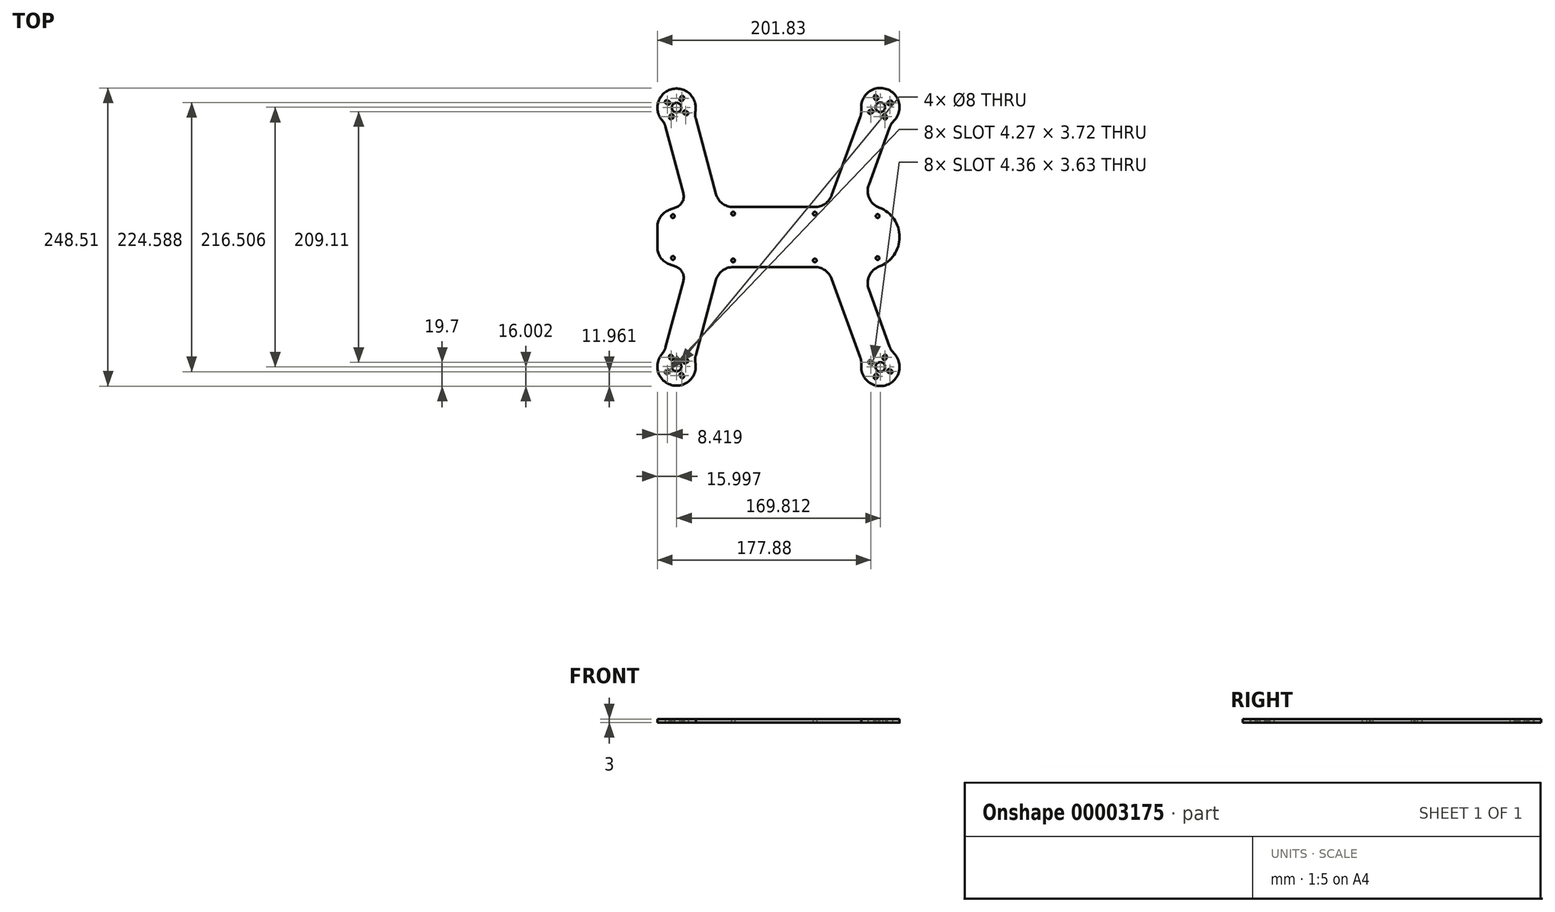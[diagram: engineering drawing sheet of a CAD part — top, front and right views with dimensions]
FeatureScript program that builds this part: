
annotation { "Feature Type Name" : "Feature", "Feature Type Description" : "" }
export const myFeature = defineFeature(function(context is Context, id is Id, definition is map)
    precondition{}
    {
        {
            var Q0;
            Q0=qCreatedBy(makeId("Top.planeOp"),FACE);
            var sketch = newSketch(context, id + "F0", { "sketchPlane" : qUnion([Q0])});
            skLineSegment(sketch, "E0", {"start": v(-72.92, 96.67) * mm, "end": v(-4.93, 96.67) * mm});
            skLineSegment(sketch, "E1", {"start": v(9.17, 106.54) * mm, "end": v(32.94, 171.87) * mm});
            skLineSegment(sketch, "E2", {"start": v(34.3, 175.6) * mm, "end": v(58.74, 166.72) * mm});
            skLineSegment(sketch, "E3", {"start": v(57.38, 162.98) * mm, "end": v(40.04, 115.35) * mm});
            skLineSegment(sketch, "E4", {"start": v(40.04, 28) * mm, "end": v(57.38, -19.63) * mm});
            skLineSegment(sketch, "E5", {"start": v(58.74, -23.37) * mm, "end": v(34.3, -32.26) * mm});
            skLineSegment(sketch, "E6", {"start": v(32.94, -28.52) * mm, "end": v(9.17, 36.8) * mm});
            skLineSegment(sketch, "E7", {"start": v(-4.93, 46.67) * mm, "end": v(-72.92, 46.67) * mm});
            skLineSegment(sketch, "E8", {"start": v(-87.4, 35.56) * mm, "end": v(-104.1, -26.76) * mm});
            skLineSegment(sketch, "E9", {"start": v(-105.13, -30.6) * mm, "end": v(-130.25, -23.87) * mm});
            skLineSegment(sketch, "E10", {"start": v(-129.22, -20.03) * mm, "end": v(-114.47, 35) * mm});
            skLineSegment(sketch, "E11", {"start": v(-114.47, 108.35) * mm, "end": v(-129.22, 163.38) * mm});
            skLineSegment(sketch, "E12", {"start": v(-130.25, 167.22) * mm, "end": v(-105.13, 173.95) * mm});
            skLineSegment(sketch, "E13", {"start": v(-104.11, 170.14) * mm, "end": v(-87.4, 107.8) * mm});
            skPoint(sketch, "E14.visualSharp", {"position": v(5.57, 96.67) * mm});
            skArc(sketch, "E14.filletArc", {"start": v(-4.93, 96.67) * mm, "mid": v(3.67, 99.39) * mm, "end": v(9.17, 106.54) * mm});
            skPoint(sketch, "E15.visualSharp", {"position": v(-84.43, 96.67) * mm});
            skArc(sketch, "E15.filletArc", {"start": v(-87.4, 107.8) * mm, "mid": v(-82.05, 99.77) * mm, "end": v(-72.92, 96.67) * mm});
            skPoint(sketch, "E16.visualSharp", {"position": v(-84.43, 46.67) * mm});
            skArc(sketch, "E16.filletArc", {"start": v(-72.92, 46.67) * mm, "mid": v(-82.05, 43.57) * mm, "end": v(-87.4, 35.56) * mm});
            skPoint(sketch, "E17.visualSharp", {"position": v(5.57, 46.67) * mm});
            skArc(sketch, "E17.filletArc", {"start": v(9.17, 36.8) * mm, "mid": v(3.67, 43.96) * mm, "end": v(-4.93, 46.67) * mm});
            skLineSegment(sketch, "E18", {"start": v(-135.56, 175.45) * mm, "end": v(-104.65, 183.73) * mm});
            skArc(sketch, "E19", {"start": v(-135.56, 175.45) * mm, "mid": v(-134.27, 172.15) * mm, "end": v(-132.28, 169.22) * mm});
            skArc(sketch, "E20", {"start": v(-104.39, 176.68) * mm, "mid": v(-104.15, 180.22) * mm, "end": v(-104.7, 183.72) * mm});
            skArc(sketch, "E21", {"start": v(-104.7, 183.72) * mm, "mid": v(-124.24, 194.94) * mm, "end": v(-135.56, 175.45) * mm});
            skPoint(sketch, "E22.visualSharp", {"position": v(-130.25, 167.22) * mm});
            skArc(sketch, "E22.filletArc", {"start": v(-129.22, 163.38) * mm, "mid": v(-130.43, 166.47) * mm, "end": v(-132.28, 169.22) * mm});
            skPoint(sketch, "E23.visualSharp", {"position": v(-105.13, 173.95) * mm});
            skArc(sketch, "E23.filletArc", {"start": v(-104.39, 176.68) * mm, "mid": v(-104.6, 173.4) * mm, "end": v(-104.11, 170.14) * mm});
            skLineSegment(sketch, "E24", {"start": v(34.67, 185.4) * mm, "end": v(64.74, 174.46) * mm});
            skArc(sketch, "E25", {"start": v(64.74, 174.46) * mm, "mid": v(55.18, 194.96) * mm, "end": v(34.67, 185.4) * mm});
            skArc(sketch, "E26", {"start": v(60.94, 168.53) * mm, "mid": v(63.17, 171.28) * mm, "end": v(64.74, 174.46) * mm});
            skArc(sketch, "E27", {"start": v(34.67, 185.4) * mm, "mid": v(33.84, 181.96) * mm, "end": v(33.78, 178.42) * mm});
            skPoint(sketch, "E28.visualSharp", {"position": v(34.3, 175.6) * mm});
            skArc(sketch, "E28.filletArc", {"start": v(32.94, 171.87) * mm, "mid": v(33.73, 175.1) * mm, "end": v(33.78, 178.42) * mm});
            skPoint(sketch, "E29.visualSharp", {"position": v(58.74, 166.72) * mm});
            skArc(sketch, "E29.filletArc", {"start": v(60.94, 168.53) * mm, "mid": v(58.85, 165.95) * mm, "end": v(57.38, 162.98) * mm});
            skLineSegment(sketch, "E30", {"start": v(34.67, -42.05) * mm, "end": v(64.74, -31.1) * mm});
            skArc(sketch, "E31", {"start": v(33.78, -35.07) * mm, "mid": v(33.84, -38.6) * mm, "end": v(34.67, -42.05) * mm});
            skArc(sketch, "E32", {"start": v(34.67, -42.05) * mm, "mid": v(55.18, -51.61) * mm, "end": v(64.74, -31.1) * mm});
            skArc(sketch, "E33", {"start": v(64.74, -31.1) * mm, "mid": v(63.17, -27.93) * mm, "end": v(60.94, -25.18) * mm});
            skPoint(sketch, "E34.visualSharp", {"position": v(58.74, -23.37) * mm});
            skArc(sketch, "E34.filletArc", {"start": v(57.38, -19.63) * mm, "mid": v(58.85, -22.6) * mm, "end": v(60.94, -25.18) * mm});
            skPoint(sketch, "E35.visualSharp", {"position": v(34.3, -32.26) * mm});
            skArc(sketch, "E35.filletArc", {"start": v(33.78, -35.07) * mm, "mid": v(33.73, -31.75) * mm, "end": v(32.94, -28.52) * mm});
            skLineSegment(sketch, "E36", {"start": v(-135.56, -32.1) * mm, "end": v(-104.65, -40.39) * mm});
            skArc(sketch, "E37", {"start": v(-135.56, -32.1) * mm, "mid": v(-124.24, -51.7) * mm, "end": v(-104.65, -40.39) * mm});
            skArc(sketch, "E38", {"start": v(-132.28, -25.87) * mm, "mid": v(-134.27, -28.8) * mm, "end": v(-135.56, -32.1) * mm});
            skArc(sketch, "E39", {"start": v(-104.65, -40.39) * mm, "mid": v(-104.12, -36.88) * mm, "end": v(-104.37, -33.35) * mm});
            skPoint(sketch, "E40.visualSharp", {"position": v(-130.25, -23.87) * mm});
            skArc(sketch, "E40.filletArc", {"start": v(-132.28, -25.87) * mm, "mid": v(-130.43, -23.12) * mm, "end": v(-129.22, -20.03) * mm});
            skPoint(sketch, "E41.visualSharp", {"position": v(-105.13, -30.6) * mm});
            skArc(sketch, "E41.filletArc", {"start": v(-104.1, -26.76) * mm, "mid": v(-104.6, -30.04) * mm, "end": v(-104.37, -33.35) * mm});
            skPoint(sketch, "E42.visualSharp", {"position": v(-112.13, 99.63) * mm});
            skPoint(sketch, "E43.visualSharp", {"position": v(-112.13, 43.72) * mm});
            skPoint(sketch, "E44", {"position": v(-123.13, 89.13) * mm});
            skCircle(sketch, "E45", {"center": v(-123.13, 89.13) * mm, "radius": 1.5 * mm});
            skPoint(sketch, "E46", {"position": v(-123.13, 54.22) * mm});
            skCircle(sketch, "E47", {"center": v(-123.13, 54.22) * mm, "radius": 1.5 * mm});
            skPoint(sketch, "E48", {"position": v(-72.92, 91.17) * mm});
            skCircle(sketch, "E49", {"center": v(-72.92, 91.17) * mm, "radius": 1.5 * mm});
            skPoint(sketch, "E50", {"position": v(-72.92, 52.17) * mm});
            skCircle(sketch, "E51", {"center": v(-72.92, 52.17) * mm, "radius": 1.5 * mm});
            skPoint(sketch, "E52", {"position": v(-4.93, 52.17) * mm});
            skCircle(sketch, "E53", {"center": v(-4.93, 52.17) * mm, "radius": 1.5 * mm});
            skPoint(sketch, "E54", {"position": v(-4.93, 91.17) * mm});
            skCircle(sketch, "E55", {"center": v(-4.93, 91.17) * mm, "radius": 1.5 * mm});
            skLineSegment(sketch, "E56", {"start": v(-113.43, 191.15) * mm, "end": v(-126.56, 168.41) * mm});
            skPoint(sketch, "E57", {"position": v(-124.1, 172.67) * mm});
            skPoint(sketch, "E58", {"position": v(-116.1, 186.52) * mm});
            skLineSegment(sketch, "E59", {"start": v(-131.69, -42.93) * mm, "end": v(-110.1, -30.47) * mm});
            skPoint(sketch, "E60", {"position": v(-113.17, -32.24) * mm});
            skPoint(sketch, "E61", {"position": v(-127.03, -40.24) * mm});
            skLineSegment(sketch, "E62", {"start": v(54.74, -25.78) * mm, "end": v(43.87, -49.1) * mm});
            skPoint(sketch, "E63", {"position": v(53.1, -29.33) * mm});
            skPoint(sketch, "E64", {"position": v(46.33, -43.83) * mm});
            skLineSegment(sketch, "E65", {"start": v(60.38, 184.9) * mm, "end": v(38.81, 174.85) * mm});
            skPoint(sketch, "E66", {"position": v(42.46, 176.55) * mm});
            skPoint(sketch, "E67", {"position": v(56.96, 183.3) * mm});
            skCircle(sketch, "E68", {"center": v(-116.1, 186.52) * mm, "radius": 1.5 * mm});
            skCircle(sketch, "E69", {"center": v(-124.1, 172.67) * mm, "radius": 1.5 * mm});
            skCircle(sketch, "E70", {"center": v(-120.1, 179.6) * mm, "radius": 4 * mm});
            skCircle(sketch, "E71", {"center": v(-113.17, -32.24) * mm, "radius": 1.5 * mm});
            skCircle(sketch, "E72", {"center": v(-120.1, -36.24) * mm, "radius": 4 * mm});
            skCircle(sketch, "E73", {"center": v(-127.03, -40.24) * mm, "radius": 1.5 * mm});
            skCircle(sketch, "E74", {"center": v(53.1, -29.33) * mm, "radius": 1.5 * mm});
            skCircle(sketch, "E75", {"center": v(49.7, -36.58) * mm, "radius": 4 * mm});
            skCircle(sketch, "E76", {"center": v(46.33, -43.83) * mm, "radius": 1.5 * mm});
            skCircle(sketch, "E77", {"center": v(49.7, 179.93) * mm, "radius": 4 * mm});
            skCircle(sketch, "E78", {"center": v(56.96, 183.3) * mm, "radius": 1.5 * mm});
            skCircle(sketch, "E79", {"center": v(42.46, 176.55) * mm, "radius": 1.5 * mm});
            skLineSegment(sketch, "E80", {"start": v(-136.08, 80.17) * mm, "end": v(-136.08, 63.17) * mm});
            skPoint(sketch, "E81", {"position": v(65.73, 71.67) * mm});
            skLineSegment(sketch, "E82", {"start": v(65.73, 71.67) * mm, "end": v(-136.08, 71.67) * mm});
            skPoint(sketch, "E83", {"position": v(-136.08, 89.67) * mm});
            skPoint(sketch, "E84", {"position": v(-136.08, 53.67) * mm});
            skLineSegment(sketch, "E85", {"start": v(-126.41, 94.2) * mm, "end": v(-120.58, 96.42) * mm});
            skLineSegment(sketch, "E86", {"start": v(-126.41, 49.15) * mm, "end": v(-120.58, 46.93) * mm});
            skArc(sketch, "E87.filletArc", {"start": v(-126.41, 94.2) * mm, "mid": v(-133.43, 88.69) * mm, "end": v(-136.08, 80.17) * mm});
            skArc(sketch, "E88.filletArc", {"start": v(-136.08, 63.17) * mm, "mid": v(-133.43, 54.66) * mm, "end": v(-126.41, 49.15) * mm});
            skArc(sketch, "E89.filletArc", {"start": v(-120.58, 96.42) * mm, "mid": v(-115.23, 101.2) * mm, "end": v(-114.47, 108.35) * mm});
            skArc(sketch, "E90.filletArc", {"start": v(-114.47, 35) * mm, "mid": v(-115.23, 42.14) * mm, "end": v(-120.58, 46.93) * mm});
            skPoint(sketch, "E91", {"position": v(-115.35, 187.82) * mm});
            skPoint(sketch, "E92", {"position": v(-124.85, 171.37) * mm});
            skCircle(sketch, "E93", {"center": v(-115.35, 187.82) * mm, "radius": 1.5 * mm});
            skCircle(sketch, "E94", {"center": v(-124.85, 171.37) * mm, "radius": 1.5 * mm});
            skLineSegment(sketch, "E95", {"start": v(-118.91, 184.66) * mm, "end": v(-115.69, 190.24) * mm});
            skLineSegment(sketch, "E96", {"start": v(-116.07, 183.57) * mm, "end": v(-113.34, 188.31) * mm});
            skLineSegment(sketch, "E97", {"start": v(-127.48, 169.81) * mm, "end": v(-125.06, 174.01) * mm});
            skLineSegment(sketch, "E98", {"start": v(-124.37, 169.2) * mm, "end": v(-122.64, 172.2) * mm});
            skPoint(sketch, "E99", {"position": v(58.32, 183.94) * mm});
            skPoint(sketch, "E100", {"position": v(41.1, 175.91) * mm});
            skCircle(sketch, "E101", {"center": v(41.1, 175.91) * mm, "radius": 1.5 * mm});
            skLineSegment(sketch, "E102", {"start": v(39.02, 176.6) * mm, "end": v(42.87, 178.4) * mm});
            skLineSegment(sketch, "E103", {"start": v(40.26, 173.87) * mm, "end": v(44.56, 175.87) * mm});
            skCircle(sketch, "E104", {"center": v(58.32, 183.94) * mm, "radius": 1.5 * mm});
            skLineSegment(sketch, "E105", {"start": v(54.7, 183.9) * mm, "end": v(58.65, 185.75) * mm});
            skLineSegment(sketch, "E106", {"start": v(56.18, 181.3) * mm, "end": v(60.7, 183.4) * mm});
            skPoint(sketch, "E107", {"position": v(53.72, -27.97) * mm});
            skCircle(sketch, "E108", {"center": v(53.72, -27.97) * mm, "radius": 1.5 * mm});
            skLineSegment(sketch, "E109", {"start": v(50.62, -31.07) * mm, "end": v(52.53, -26.98) * mm});
            skLineSegment(sketch, "E110", {"start": v(53.5, -32) * mm, "end": v(55.61, -27.47) * mm});
            skPoint(sketch, "E111", {"position": v(45.7, -45.19) * mm});
            skCircle(sketch, "E112", {"center": v(45.7, -45.19) * mm, "radius": 1.5 * mm});
            skLineSegment(sketch, "E113", {"start": v(43.25, -46.9) * mm, "end": v(45.34, -42.4) * mm});
            skLineSegment(sketch, "E114", {"start": v(46.2, -47.66) * mm, "end": v(48.31, -43.12) * mm});
            skPoint(sketch, "E115", {"position": v(-111.88, -31.5) * mm});
            skCircle(sketch, "E116", {"center": v(-111.88, -31.5) * mm, "radius": 1.5 * mm});
            skLineSegment(sketch, "E117", {"start": v(-116.41, -32.38) * mm, "end": v(-112.12, -29.9) * mm});
            skLineSegment(sketch, "E118", {"start": v(-114.3, -34.63) * mm, "end": v(-109.74, -32) * mm});
            skPoint(sketch, "E119", {"position": v(-128.33, -41) * mm});
            skCircle(sketch, "E120", {"center": v(-128.33, -41) * mm, "radius": 1.5 * mm});
            skLineSegment(sketch, "E121", {"start": v(-131.8, -41.27) * mm, "end": v(-127.15, -38.58) * mm});
            skLineSegment(sketch, "E122", {"start": v(-130, -43.7) * mm, "end": v(-124.48, -40.5) * mm});
            skArc(sketch, "E123", {"start": v(48.81, 47.15) * mm, "mid": v(65.73, 71.67) * mm, "end": v(48.81, 96.2) * mm});
            skPoint(sketch, "E124.visualSharp", {"position": v(33.43, 97.2) * mm});
            skArc(sketch, "E124.filletArc", {"start": v(40.04, 115.35) * mm, "mid": v(40.5, 103.98) * mm, "end": v(48.81, 96.2) * mm});
            skPoint(sketch, "E125.visualSharp", {"position": v(33.43, 46.15) * mm});
            skArc(sketch, "E125.filletArc", {"start": v(48.81, 47.15) * mm, "mid": v(40.5, 39.37) * mm, "end": v(40.04, 28) * mm});
            skPoint(sketch, "E126", {"position": v(-71.08, 71.67) * mm});
            skPoint(sketch, "E127", {"position": v(-67.08, 71.67) * mm});
            skPoint(sketch, "E128", {"position": v(42.92, 71.67) * mm});
            skPoint(sketch, "E129", {"position": v(46.73, 71.67) * mm});
            skPoint(sketch, "E130", {"position": v(-71.08, 89.67) * mm});
            skPoint(sketch, "E131", {"position": v(-71.08, 53.67) * mm});
            skLineSegment(sketch, "E132.bottom", {"start": v(-71.08, 53.67) * mm, "end": v(-131.08, 53.67) * mm});
            skLineSegment(sketch, "E132.top", {"start": v(-71.08, 89.67) * mm, "end": v(-131.08, 89.67) * mm});
            skLineSegment(sketch, "E132.left", {"start": v(-71.08, 53.67) * mm, "end": v(-71.08, 89.67) * mm});
            skLineSegment(sketch, "E132.right", {"start": v(-131.08, 53.67) * mm, "end": v(-131.08, 89.67) * mm});
            skLineSegment(sketch, "E133.bottom", {"start": v(-67.08, 53.67) * mm, "end": v(42.92, 53.67) * mm});
            skLineSegment(sketch, "E133.top", {"start": v(-67.08, 89.67) * mm, "end": v(42.92, 89.67) * mm});
            skLineSegment(sketch, "E133.left", {"start": v(-67.08, 53.67) * mm, "end": v(-67.08, 89.67) * mm});
            skLineSegment(sketch, "E133.right", {"start": v(42.92, 53.67) * mm, "end": v(42.92, 89.67) * mm});
            skPoint(sketch, "E134", {"position": v(-67.08, 53.67) * mm});
            skLineSegment(sketch, "E135.bottom", {"start": v(48.73, 66.67) * mm, "end": v(56.73, 66.67) * mm});
            skLineSegment(sketch, "E135.top", {"start": v(48.73, 76.67) * mm, "end": v(56.73, 76.67) * mm});
            skLineSegment(sketch, "E135.left", {"start": v(46.73, 68.67) * mm, "end": v(46.73, 74.67) * mm});
            skLineSegment(sketch, "E135.right", {"start": v(58.73, 68.67) * mm, "end": v(58.73, 74.67) * mm});
            skPoint(sketch, "E136", {"position": v(46.73, 66.67) * mm});
            skPoint(sketch, "E137.visualSharp", {"position": v(58.73, 76.67) * mm});
            skArc(sketch, "E137.filletArc", {"start": v(58.73, 74.67) * mm, "mid": v(58.15, 76.09) * mm, "end": v(56.73, 76.67) * mm});
            skPoint(sketch, "E138.visualSharp", {"position": v(46.73, 76.67) * mm});
            skArc(sketch, "E138.filletArc", {"start": v(48.73, 76.67) * mm, "mid": v(47.32, 76.09) * mm, "end": v(46.73, 74.67) * mm});
            skArc(sketch, "E139.filletArc", {"start": v(46.73, 68.67) * mm, "mid": v(47.32, 67.26) * mm, "end": v(48.73, 66.67) * mm});
            skPoint(sketch, "E140.visualSharp", {"position": v(58.73, 66.67) * mm});
            skArc(sketch, "E140.filletArc", {"start": v(56.73, 66.67) * mm, "mid": v(58.15, 67.26) * mm, "end": v(58.73, 68.67) * mm});
            skPoint(sketch, "E141", {"position": v(47.43, 89.2) * mm});
            skPoint(sketch, "E142", {"position": v(47.43, 54.15) * mm});
            skCircle(sketch, "E143", {"center": v(47.43, 89.2) * mm, "radius": 1.5 * mm});
            skCircle(sketch, "E144", {"center": v(47.43, 54.15) * mm, "radius": 1.5 * mm});
            skCircle(sketch, "E145", {"center": v(-120.1, 179.6) * mm, "radius": 76.2 * mm});
            skCircle(sketch, "E146", {"center": v(49.7, 179.93) * mm, "radius": 76.2 * mm});
            skLineSegment(sketch, "E147", {"start": v(-109.34, 173.38) * mm, "end": v(-131.52, 186.19) * mm});
            skPoint(sketch, "E148", {"position": v(-113.17, 175.6) * mm});
            skPoint(sketch, "E149", {"position": v(-111.88, 174.84) * mm});
            skPoint(sketch, "E150", {"position": v(-127.03, 183.6) * mm});
            skPoint(sketch, "E151", {"position": v(-128.33, 184.34) * mm});
            skCircle(sketch, "E152", {"center": v(-113.17, 175.6) * mm, "radius": 1.5 * mm});
            skCircle(sketch, "E153", {"center": v(-111.88, 174.84) * mm, "radius": 1.5 * mm});
            skCircle(sketch, "E154", {"center": v(-127.03, 183.6) * mm, "radius": 1.5 * mm});
            skCircle(sketch, "E155", {"center": v(-128.33, 184.34) * mm, "radius": 1.5 * mm});
            skLineSegment(sketch, "E156", {"start": v(-126.05, 181.3) * mm, "end": v(-130.87, 184.08) * mm});
            skLineSegment(sketch, "E157", {"start": v(-124.14, 183.66) * mm, "end": v(-128.75, 186.32) * mm});
            skLineSegment(sketch, "E158", {"start": v(-115.27, 175.07) * mm, "end": v(-111.76, 173.05) * mm});
            skLineSegment(sketch, "E159", {"start": v(-109.07, 174.95) * mm, "end": v(-113.61, 177.58) * mm});
            skLineSegment(sketch, "E160", {"start": v(43.8, 192.62) * mm, "end": v(54.9, 168.8) * mm});
            skPoint(sketch, "E161", {"position": v(46.33, 187.18) * mm});
            skPoint(sketch, "E162", {"position": v(45.7, 188.54) * mm});
            skPoint(sketch, "E163", {"position": v(53.1, 172.68) * mm});
            skPoint(sketch, "E164", {"position": v(53.72, 171.32) * mm});
            skCircle(sketch, "E165", {"center": v(45.7, 188.54) * mm, "radius": 1.5 * mm});
            skCircle(sketch, "E166", {"center": v(46.33, 187.18) * mm, "radius": 1.5 * mm});
            skCircle(sketch, "E167", {"center": v(53.1, 172.68) * mm, "radius": 1.5 * mm});
            skCircle(sketch, "E168", {"center": v(53.72, 171.32) * mm, "radius": 1.5 * mm});
            skLineSegment(sketch, "E169", {"start": v(42.64, 191.53) * mm, "end": v(45.81, 184.74) * mm});
            skLineSegment(sketch, "E170", {"start": v(45.8, 191.86) * mm, "end": v(48.98, 185.03) * mm});
            skLineSegment(sketch, "E171", {"start": v(50.66, 174.34) * mm, "end": v(53.37, 168.52) * mm});
            skLineSegment(sketch, "E172", {"start": v(53.4, 175.54) * mm, "end": v(56.44, 169.05) * mm});
            skLineSegment(sketch, "E173", {"start": v(-112.78, -48.93) * mm, "end": v(-127.5, -23.43) * mm});
            skPoint(sketch, "E174", {"position": v(-124.1, -29.32) * mm});
            skPoint(sketch, "E175", {"position": v(-124.85, -28.02) * mm});
            skPoint(sketch, "E176", {"position": v(-116.1, -43.17) * mm});
            skPoint(sketch, "E177", {"position": v(-115.35, -44.47) * mm});
            skCircle(sketch, "E178", {"center": v(-116.1, -43.17) * mm, "radius": 1.5 * mm});
            skCircle(sketch, "E179", {"center": v(-115.35, -44.47) * mm, "radius": 1.5 * mm});
            skCircle(sketch, "E180", {"center": v(-124.85, -28.02) * mm, "radius": 1.5 * mm});
            skCircle(sketch, "E181", {"center": v(-124.1, -29.32) * mm, "radius": 1.5 * mm});
            skLineSegment(sketch, "E182", {"start": v(-127.3, -26.79) * mm, "end": v(-124.04, -32.42) * mm});
            skLineSegment(sketch, "E183", {"start": v(-124.1, -26.32) * mm, "end": v(-121.82, -30.27) * mm});
            skLineSegment(sketch, "E184", {"start": v(-118.47, -42.07) * mm, "end": v(-115.64, -46.98) * mm});
            skLineSegment(sketch, "E185", {"start": v(-115.69, -40.89) * mm, "end": v(-113, -45.56) * mm});
            skLineSegment(sketch, "E186", {"start": v(40, -32.05) * mm, "end": v(62.3, -42.45) * mm});
            skPoint(sketch, "E187", {"position": v(42.46, -33.2) * mm});
            skPoint(sketch, "E188", {"position": v(41.1, -32.56) * mm});
            skPoint(sketch, "E189", {"position": v(56.96, -39.96) * mm});
            skPoint(sketch, "E190", {"position": v(58.32, -40.6) * mm});
            skCircle(sketch, "E191", {"center": v(56.96, -39.96) * mm, "radius": 1.5 * mm});
            skCircle(sketch, "E192", {"center": v(58.32, -40.6) * mm, "radius": 1.5 * mm});
            skCircle(sketch, "E193", {"center": v(42.46, -33.2) * mm, "radius": 1.5 * mm});
            skCircle(sketch, "E194", {"center": v(41.1, -32.56) * mm, "radius": 1.5 * mm});
            skLineSegment(sketch, "E195", {"start": v(38.12, -32.83) * mm, "end": v(43.6, -35.38) * mm});
            skLineSegment(sketch, "E196", {"start": v(40.36, -30.56) * mm, "end": v(44.72, -32.6) * mm});
            skLineSegment(sketch, "E197", {"start": v(56.42, -38.05) * mm, "end": v(61.4, -40.38) * mm});
            skLineSegment(sketch, "E198", {"start": v(54.5, -40.47) * mm, "end": v(60.2, -43.13) * mm});
            skSolve(sketch);
        }
        {
            var Q0;
            {var subQ11=sQuery(id+"F0.wireOp",EDGE,"E21");Q0=makeQuery(id+"F0.imprint","IMPRINT",FACE,{"disambiguationData":[TD([[makeQuery(id+"F0.imprint","IMPRINT",EDGE,{"derivedFrom":subQ11}),1.0]])]});}
            var Q1;
            {var subQ23=sQuery(id+"F0.wireOp",EDGE,"E11");Q1=makeQuery(id+"F0.imprint","IMPRINT",FACE,{"disambiguationData":[TD([[makeQuery(id+"F0.imprint","IMPRINT",EDGE,{"derivedFrom":subQ23}),-1.0]])]});}
            var Q2;
            Q2=makeQuery(id+"F0.imprint","IMPRINT",FACE,{"disambiguationData":[TD([[makeQuery(id+"F0.imprint","IMPRINT",EDGE,{"derivedFrom":sQuery(id+"F0.wireOp",EDGE,"E0")}),-1.0]])]});
            var Q3;
            {var subQ3=sQuery(id+"F0.wireOp",EDGE,"E132.top");var subQ8=sQuery(id+"F0.wireOp",EDGE,"E45");var subQ10=makeQuery(id+"F0.imprint","INTERSECT",VERTEX,{"disambiguationData":[OD(0.0)],"derivedFrom":[subQ8,subQ3]});Q3=makeQuery(id+"F0.imprint","IMPRINT",FACE,{"disambiguationData":[TD([[makeQuery(id+"F0.imprint","IMPRINT",EDGE,{"disambiguationData":[TD([[subQ10,1.0]])],"derivedFrom":subQ8}),-1.0]])]});}
            var Q4;
            {var subQ3=sQuery(id+"F0.wireOp",EDGE,"E132.bottom");var subQ8=sQuery(id+"F0.wireOp",EDGE,"E47");var subQ10=makeQuery(id+"F0.imprint","INTERSECT",VERTEX,{"disambiguationData":[OD(0.0)],"derivedFrom":[subQ8,subQ3]});Q4=makeQuery(id+"F0.imprint","IMPRINT",FACE,{"disambiguationData":[TD([[makeQuery(id+"F0.imprint","IMPRINT",EDGE,{"disambiguationData":[TD([[subQ10,-1.0]])],"derivedFrom":subQ8}),-1.0]])]});}
            var Q5;
            Q5=makeQuery(id+"F0.imprint","IMPRINT",FACE,{"disambiguationData":[TD([[makeQuery(id+"F0.imprint","IMPRINT",EDGE,{"derivedFrom":sQuery(id+"F0.wireOp",EDGE,"E4")}),-1.0]])]});
            var Q6;
            {var subQ0=sQuery(id+"F0.wireOp",EDGE,"E133.right");var subQ1=sQuery(id+"F0.wireOp",EDGE,"E82");var subQ2=makeQuery(id+"F0.imprint","INTERSECT",VERTEX,{"derivedFrom":[subQ1,subQ0]});Q6=makeQuery(id+"F0.imprint","IMPRINT",FACE,{"disambiguationData":[TD([[makeQuery(id+"F0.imprint","IMPRINT",EDGE,{"disambiguationData":[TD([[subQ2,-1.0]])],"derivedFrom":subQ1}),1.0]])]});}
            var Q7;
            {var subQ0=sQuery(id+"F0.wireOp",EDGE,"E133.right");var subQ1=sQuery(id+"F0.wireOp",EDGE,"E82");var subQ2=makeQuery(id+"F0.imprint","INTERSECT",VERTEX,{"derivedFrom":[subQ1,subQ0]});Q7=makeQuery(id+"F0.imprint","IMPRINT",FACE,{"disambiguationData":[TD([[makeQuery(id+"F0.imprint","IMPRINT",EDGE,{"disambiguationData":[TD([[subQ2,-1.0]])],"derivedFrom":subQ1}),-1.0]])]});}
            var Q8;
            {var subQ17=sQuery(id+"F0.wireOp",EDGE,"E3");Q8=makeQuery(id+"F0.imprint","IMPRINT",FACE,{"disambiguationData":[TD([[makeQuery(id+"F0.imprint","IMPRINT",EDGE,{"derivedFrom":subQ17}),-1.0]])]});}
            var Q9;
            {var subQ13=sQuery(id+"F0.wireOp",EDGE,"E25");Q9=makeQuery(id+"F0.imprint","IMPRINT",FACE,{"disambiguationData":[TD([[makeQuery(id+"F0.imprint","IMPRINT",EDGE,{"derivedFrom":subQ13}),1.0]])]});}
            var Q10;
            {var subQ11=sQuery(id+"F0.wireOp",EDGE,"E32");Q10=makeQuery(id+"F0.imprint","IMPRINT",FACE,{"disambiguationData":[TD([[makeQuery(id+"F0.imprint","IMPRINT",EDGE,{"derivedFrom":subQ11}),1.0]])]});}
            var Q11;
            {var subQ12=sQuery(id+"F0.wireOp",EDGE,"E37");Q11=makeQuery(id+"F0.imprint","IMPRINT",FACE,{"disambiguationData":[TD([[makeQuery(id+"F0.imprint","IMPRINT",EDGE,{"derivedFrom":subQ12}),1.0]])]});}
            var Q12;
            Q12=makeQuery(id+"F0.imprint","IMPRINT",FACE,{"disambiguationData":[TD([[makeQuery(id+"F0.imprint","IMPRINT",EDGE,{"derivedFrom":sQuery(id+"F0.wireOp",EDGE,"E135.top")}),-1.0]])]});
            var Q13;
            Q13=makeQuery(id+"F0.imprint","IMPRINT",FACE,{"disambiguationData":[TD([[makeQuery(id+"F0.imprint","IMPRINT",EDGE,{"derivedFrom":sQuery(id+"F0.wireOp",EDGE,"E135.bottom")}),1.0]])]});
            var Q14;
            {var subQ17=sQuery(id+"F0.wireOp",EDGE,"E3");Q14=makeQuery(id+"F0.imprint","IMPRINT",FACE,{"disambiguationData":[TD([[makeQuery(id+"F0.imprint","IMPRINT",EDGE,{"derivedFrom":subQ17}),-1.0]])]});}
            extrude(context, id + "F1", {"entities" : qUnion([Q0, Q1, Q2, Q3, Q4, Q5, Q6, Q7, Q8, Q9, Q10, Q11, Q12, Q13, Q14]), "depth" : 3 * mm});
        }
    });
